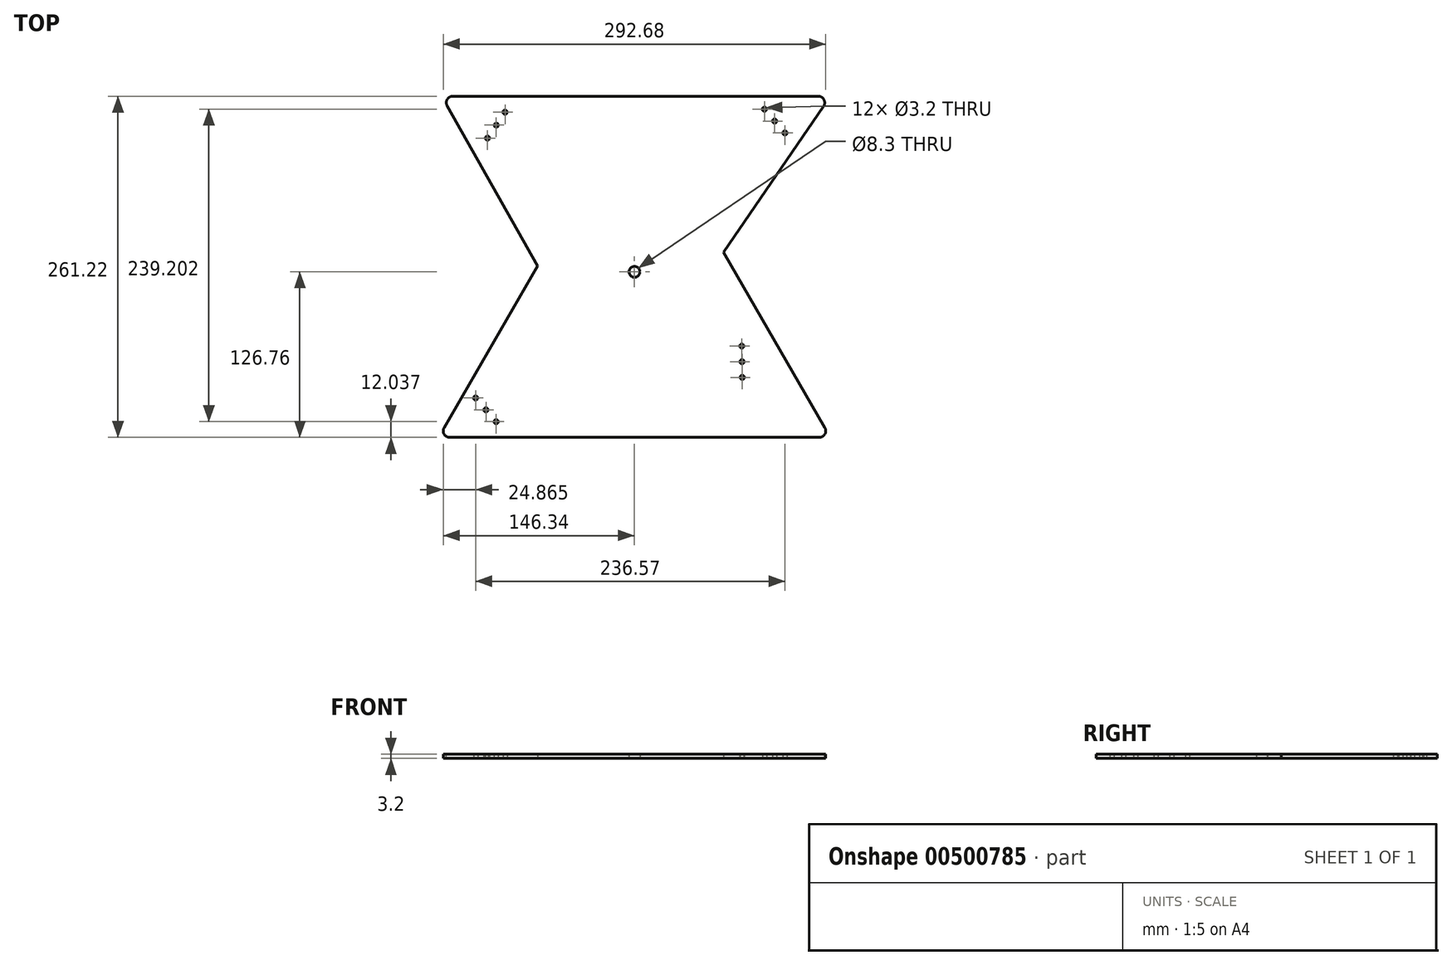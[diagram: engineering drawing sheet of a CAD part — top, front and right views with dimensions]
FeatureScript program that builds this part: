
annotation { "Feature Type Name" : "Feature", "Feature Type Description" : "" }
export const myFeature = defineFeature(function(context is Context, id is Id, definition is map)
    precondition{}
    {
        {
            var Q0;
            Q0=qCreatedBy(makeId("Top.planeOp"),FACE);
            var sketch = newSketch(context, id + "F0", { "sketchPlane" : qUnion([Q0])});
            skLineSegment(sketch, "E0", {"start": v(-150, -126.76) * mm, "end": v(150, -126.76) * mm});
            skLineSegment(sketch, "E1", {"start": v(-150, -126.76) * mm, "end": v(0, 133.04) * mm});
            skLineSegment(sketch, "E2", {"start": v(0, 133.04) * mm, "end": v(150, -126.76) * mm});
            skLineSegment(sketch, "E3.top", {"start": v(-147.51, 134.46) * mm, "end": v(150, 134.46) * mm});
            skCircle(sketch, "E4", {"center": v(0, 0) * mm, "radius": 55 * mm});
            skCircle(sketch, "E5", {"center": v(0, 0) * mm, "radius": 4.15 * mm});
            skLineSegment(sketch, "E6", {"start": v(-150, -126.76) * mm, "end": v(-74.17, 4.58) * mm});
            skLineSegment(sketch, "E7", {"start": v(-74.17, 4.58) * mm, "end": v(0, 133.04) * mm});
            skLineSegment(sketch, "E8", {"start": v(-147.51, 134.46) * mm, "end": v(-74.17, 4.58) * mm});
            skLineSegment(sketch, "E9", {"start": v(-74.17, 4.58) * mm, "end": v(0, -126.76) * mm});
            skLineSegment(sketch, "E10", {"start": v(0, -126.76) * mm, "end": v(68.22, 14.9) * mm});
            skLineSegment(sketch, "E11", {"start": v(68.22, 14.9) * mm, "end": v(150, 134.46) * mm});
            skLineSegment(sketch, "E12", {"start": v(-103.6, 96.31) * mm, "end": v(-121.38, 108.4) * mm});
            skLineSegment(sketch, "E13", {"start": v(-121.38, 108.4) * mm, "end": v(-107.89, 128.24) * mm});
            skLineSegment(sketch, "E14", {"start": v(-90.1, 116.16) * mm, "end": v(-107.89, 128.24) * mm});
            skLineSegment(sketch, "E15", {"start": v(-103.6, 96.31) * mm, "end": v(-90.1, 116.16) * mm});
            skLineSegment(sketch, "E16", {"start": v(-114.63, 118.32) * mm, "end": v(-96.85, 106.24) * mm});
            skLineSegment(sketch, "E17", {"start": v(-99, 122.2) * mm, "end": v(-112.49, 102.35) * mm});
            skCircle(sketch, "E18", {"center": v(-105.74, 112.28) * mm, "radius": 1.6 * mm});
            skCircle(sketch, "E19", {"center": v(-99, 122.2) * mm, "radius": 1.6 * mm});
            skCircle(sketch, "E20", {"center": v(-112.49, 102.35) * mm, "radius": 1.6 * mm});
            skLineSegment(sketch, "E21", {"start": v(-97.65, -107.7) * mm, "end": v(-113.93, -121.75) * mm});
            skLineSegment(sketch, "E22", {"start": v(-113.93, -121.75) * mm, "end": v(-129.61, -103.58) * mm});
            skLineSegment(sketch, "E23", {"start": v(-113.34, -89.53) * mm, "end": v(-129.61, -103.58) * mm});
            skLineSegment(sketch, "E24", {"start": v(-97.65, -107.7) * mm, "end": v(-113.34, -89.53) * mm});
            skLineSegment(sketch, "E25", {"start": v(-121.77, -112.66) * mm, "end": v(-105.5, -98.61) * mm});
            skLineSegment(sketch, "E26", {"start": v(-121.47, -96.56) * mm, "end": v(-105.8, -114.72) * mm});
            skCircle(sketch, "E27", {"center": v(-113.63, -105.64) * mm, "radius": 1.6 * mm});
            skCircle(sketch, "E28", {"center": v(-121.47, -96.56) * mm, "radius": 1.6 * mm});
            skCircle(sketch, "E29", {"center": v(-105.8, -114.72) * mm, "radius": 1.6 * mm});
            skLineSegment(sketch, "E30", {"start": v(123.23, 113.34) * mm, "end": v(106.96, 99.29) * mm});
            skLineSegment(sketch, "E31", {"start": v(106.96, 99.29) * mm, "end": v(91.28, 117.45) * mm});
            skLineSegment(sketch, "E32", {"start": v(107.55, 131.5) * mm, "end": v(91.28, 117.45) * mm});
            skLineSegment(sketch, "E33", {"start": v(123.23, 113.34) * mm, "end": v(107.55, 131.5) * mm});
            skLineSegment(sketch, "E34", {"start": v(99.12, 108.37) * mm, "end": v(115.4, 122.42) * mm});
            skLineSegment(sketch, "E35", {"start": v(99.41, 124.48) * mm, "end": v(115.1, 106.31) * mm});
            skCircle(sketch, "E36", {"center": v(107.25, 115.4) * mm, "radius": 1.6 * mm});
            skCircle(sketch, "E37", {"center": v(99.41, 124.48) * mm, "radius": 1.6 * mm});
            skCircle(sketch, "E38", {"center": v(115.1, 106.31) * mm, "radius": 1.6 * mm});
            skCircle(sketch, "E39", {"center": v(82.28, -68.83) * mm, "radius": 1.6 * mm});
            skCircle(sketch, "E40", {"center": v(82.11, -56.83) * mm, "radius": 1.6 * mm});
            skCircle(sketch, "E41", {"center": v(82.45, -80.83) * mm, "radius": 1.6 * mm});
            skSolve(sketch);
        }
        {
            var Q0;
            {var subQ0=sQuery(id+"F0.wireOp",EDGE,"E3.bottom");var subQ1=sQuery(id+"F0.wireOp",EDGE,"E1");var subQ2=makeQuery(id+"F0.imprint","INTERSECT",VERTEX,{"derivedFrom":[subQ1,subQ0]});Q0=makeQuery(id+"F0.imprint","IMPRINT",FACE,{"disambiguationData":[TD([[makeQuery(id+"F0.imprint","IMPRINT",EDGE,{"disambiguationData":[TD([[subQ2,-1.0]])],"derivedFrom":subQ1}),-1.0]])]});}
            var Q1;
            {var subQ0=sQuery(id+"F0.wireOp",EDGE,"E4");var subQ1=sQuery(id+"F0.wireOp",EDGE,"E1");var subQ2=makeQuery(id+"F0.imprint","INTERSECT",VERTEX,{"disambiguationData":[OD(0.0)],"derivedFrom":[subQ1,subQ0]});Q1=makeQuery(id+"F0.imprint","IMPRINT",FACE,{"disambiguationData":[TD([[makeQuery(id+"F0.imprint","IMPRINT",EDGE,{"disambiguationData":[TD([[subQ2,-1.0]])],"derivedFrom":subQ1}),1.0]])]});}
            var Q2;
            {var subQ0=sQuery(id+"F0.wireOp",EDGE,"E4");var subQ1=sQuery(id+"F0.wireOp",EDGE,"E2");var subQ2=makeQuery(id+"F0.imprint","INTERSECT",VERTEX,{"disambiguationData":[OD(0.0)],"derivedFrom":[subQ1,subQ0]});Q2=makeQuery(id+"F0.imprint","IMPRINT",FACE,{"disambiguationData":[TD([[makeQuery(id+"F0.imprint","IMPRINT",EDGE,{"disambiguationData":[TD([[subQ2,1.0]])],"derivedFrom":subQ1}),1.0]])]});}
            var Q3;
            {var subQ0=sQuery(id+"F0.wireOp",EDGE,"E3.bottom");var subQ1=sQuery(id+"F0.wireOp",EDGE,"E2");var subQ2=makeQuery(id+"F0.imprint","INTERSECT",VERTEX,{"derivedFrom":[subQ1,subQ0]});Q3=makeQuery(id+"F0.imprint","IMPRINT",FACE,{"disambiguationData":[TD([[makeQuery(id+"F0.imprint","IMPRINT",EDGE,{"disambiguationData":[TD([[subQ2,1.0]])],"derivedFrom":subQ1}),-1.0]])]});}
            var Q4;
            {var subQ1=sQuery(id+"F0.wireOp",EDGE,"rkFMjEgM-NqXY-omBp-b8pJ-evcCWdkULaWJ");var subQ3=sQuery(id+"F0.wireOp",EDGE,"E4");var subQ4=makeQuery(id+"F0.imprint","INTERSECT",VERTEX,{"disambiguationData":[OD(1.0)],"derivedFrom":[subQ1,subQ3]});Q4=makeQuery(id+"F0.imprint","IMPRINT",FACE,{"disambiguationData":[TD([[makeQuery(id+"F0.imprint","IMPRINT",EDGE,{"disambiguationData":[TD([[subQ4,-1.0]])],"derivedFrom":subQ3}),-1.0]])]});}
            var Q5;
            {var subQ1=sQuery(id+"F0.wireOp",EDGE,"cOxABnS7-H8AW-JM4u-R3lf-1G958eR7zzaA");var subQ3=sQuery(id+"F0.wireOp",EDGE,"E4");var subQ4=makeQuery(id+"F0.imprint","INTERSECT",VERTEX,{"disambiguationData":[OD(1.0)],"derivedFrom":[subQ1,subQ3]});Q5=makeQuery(id+"F0.imprint","IMPRINT",FACE,{"disambiguationData":[TD([[makeQuery(id+"F0.imprint","IMPRINT",EDGE,{"disambiguationData":[TD([[subQ4,-1.0]])],"derivedFrom":subQ3}),-1.0]])]});}
            var Q6;
            {var subQ1=sQuery(id+"F0.wireOp",EDGE,"E3.top");Q6=makeQuery(id+"F0.imprint","IMPRINT",FACE,{"disambiguationData":[TD([[makeQuery(id+"F0.imprint","IMPRINT",EDGE,{"derivedFrom":subQ1}),-1.0]])]});}
            var Q7;
            {var subQ1=sQuery(id+"F0.wireOp",EDGE,"E1");var subQ3=sQuery(id+"F0.wireOp",EDGE,"E4");var subQ4=makeQuery(id+"F0.imprint","INTERSECT",VERTEX,{"disambiguationData":[OD(1.0)],"derivedFrom":[subQ1,subQ3]});Q7=makeQuery(id+"F0.imprint","IMPRINT",FACE,{"disambiguationData":[TD([[makeQuery(id+"F0.imprint","IMPRINT",EDGE,{"disambiguationData":[TD([[subQ4,1.0]])],"derivedFrom":subQ3}),-1.0]])]});}
            var Q8;
            {var subQ1=sQuery(id+"F0.wireOp",EDGE,"E2");var subQ3=sQuery(id+"F0.wireOp",EDGE,"E4");var subQ4=makeQuery(id+"F0.imprint","INTERSECT",VERTEX,{"disambiguationData":[OD(1.0)],"derivedFrom":[subQ1,subQ3]});Q8=makeQuery(id+"F0.imprint","IMPRINT",FACE,{"disambiguationData":[TD([[makeQuery(id+"F0.imprint","IMPRINT",EDGE,{"disambiguationData":[TD([[subQ4,-1.0]])],"derivedFrom":subQ3}),-1.0]])]});}
            var Q9;
            {var subQ24=sQuery(id+"F0.wireOp",EDGE,"3a51rPi0-I0Z5-NmN3-UwWW-pAn3P1ib9wdr");Q9=makeQuery(id+"F0.imprint","IMPRINT",FACE,{"disambiguationData":[TD([[makeQuery(id+"F0.imprint","IMPRINT",EDGE,{"derivedFrom":subQ24}),-1.0]])]});}
            var Q10;
            {var subQ1=sQuery(id+"F0.wireOp",EDGE,"fhWdT4TT-t5z4-IOB7-9m6H-m55lK3yafObH");var subQ6=sQuery(id+"F0.wireOp",EDGE,"V1MSOyJx-UlwA-KniW-Hypj-Iz20MsfqlTOy");var subQ9=makeQuery(id+"F0.imprint","INTERSECT",VERTEX,{"derivedFrom":[subQ6,subQ1]});Q10=makeQuery(id+"F0.imprint","IMPRINT",FACE,{"disambiguationData":[TD([[makeQuery(id+"F0.imprint","IMPRINT",EDGE,{"disambiguationData":[TD([[subQ9,1.0]])],"derivedFrom":subQ6}),-1.0]])]});}
            var Q11;
            {var subQ0=sQuery(id+"F0.wireOp",EDGE,"YwnaRzwQ-0DJ0-LU4o-7aIr-p4F8uUAJ6yCD");var subQ1=sQuery(id+"F0.wireOp",EDGE,"fhWdT4TT-t5z4-IOB7-9m6H-m55lK3yafObH");var subQ2=makeQuery(id+"F0.imprint","INTERSECT",VERTEX,{"derivedFrom":[subQ1,subQ0]});Q11=makeQuery(id+"F0.imprint","IMPRINT",FACE,{"disambiguationData":[TD([[makeQuery(id+"F0.imprint","IMPRINT",EDGE,{"disambiguationData":[TD([[subQ2,-1.0]])],"derivedFrom":subQ1}),1.0]])]});}
            var Q12;
            {var subQ1=sQuery(id+"F0.wireOp",EDGE,"fhWdT4TT-t5z4-IOB7-9m6H-m55lK3yafObH");var subQ5=sQuery(id+"F0.wireOp",EDGE,"YwnaRzwQ-0DJ0-LU4o-7aIr-p4F8uUAJ6yCD");var subQ6=makeQuery(id+"F0.imprint","INTERSECT",VERTEX,{"derivedFrom":[subQ1,subQ5]});Q12=makeQuery(id+"F0.imprint","IMPRINT",FACE,{"disambiguationData":[TD([[makeQuery(id+"F0.imprint","IMPRINT",EDGE,{"disambiguationData":[TD([[subQ6,1.0]])],"derivedFrom":subQ1}),1.0]])]});}
            var Q13;
            {var subQ3=sQuery(id+"F0.wireOp",EDGE,"ZtclyvMB-XdF3-0tLt-WoJ9-w7VQqLJZLKuw");var subQ7=sQuery(id+"F0.wireOp",EDGE,"sQT1DKzU-x4bm-HVrY-kuNr-4rAKIQ2P2SoH");var subQ9=makeQuery(id+"F0.imprint","INTERSECT",VERTEX,{"disambiguationData":[OD(1.0)],"derivedFrom":[subQ7,subQ3]});Q13=makeQuery(id+"F0.imprint","IMPRINT",FACE,{"disambiguationData":[TD([[makeQuery(id+"F0.imprint","IMPRINT",EDGE,{"disambiguationData":[TD([[subQ9,-1.0]])],"derivedFrom":subQ7}),1.0]])]});}
            var Q14;
            {var subQ1=sQuery(id+"F0.wireOp",EDGE,"lj4hX3Zr-Y8O4-Ni6O-LBAL-KsnYeP7ui8yA");var subQ5=sQuery(id+"F0.wireOp",EDGE,"8QxvuuJz-OpXC-lB6l-rkeD-zr6WuXKeRFd8");var subQ6=makeQuery(id+"F0.imprint","INTERSECT",VERTEX,{"derivedFrom":[subQ1,subQ5]});Q14=makeQuery(id+"F0.imprint","IMPRINT",FACE,{"disambiguationData":[TD([[makeQuery(id+"F0.imprint","IMPRINT",EDGE,{"disambiguationData":[TD([[subQ6,-1.0]])],"derivedFrom":subQ1}),-1.0]])]});}
            var Q15;
            {var subQ5=sQuery(id+"F0.wireOp",EDGE,"YwnaRzwQ-0DJ0-LU4o-7aIr-p4F8uUAJ6yCD");var subQ7=sQuery(id+"F0.wireOp",EDGE,"sQT1DKzU-x4bm-HVrY-kuNr-4rAKIQ2P2SoH");var subQ8=makeQuery(id+"F0.imprint","INTERSECT",VERTEX,{"derivedFrom":[subQ7,subQ5]});Q15=makeQuery(id+"F0.imprint","IMPRINT",FACE,{"disambiguationData":[TD([[makeQuery(id+"F0.imprint","IMPRINT",EDGE,{"disambiguationData":[TD([[subQ8,-1.0]])],"derivedFrom":subQ7}),1.0]])]});}
            var Q16;
            {var subQ1=sQuery(id+"F0.wireOp",EDGE,"lj4hX3Zr-Y8O4-Ni6O-LBAL-KsnYeP7ui8yA");var subQ6=sQuery(id+"F0.wireOp",EDGE,"V1MSOyJx-UlwA-KniW-Hypj-Iz20MsfqlTOy");var subQ9=makeQuery(id+"F0.imprint","INTERSECT",VERTEX,{"derivedFrom":[subQ1,subQ6]});Q16=makeQuery(id+"F0.imprint","IMPRINT",FACE,{"disambiguationData":[TD([[makeQuery(id+"F0.imprint","IMPRINT",EDGE,{"disambiguationData":[TD([[subQ9,1.0]])],"derivedFrom":subQ1}),-1.0]])]});}
            var Q17;
            {var subQ0=sQuery(id+"F0.wireOp",EDGE,"E4");var subQ1=sQuery(id+"F0.wireOp",EDGE,"E1");var subQ2=makeQuery(id+"F0.imprint","INTERSECT",VERTEX,{"disambiguationData":[OD(0.0)],"derivedFrom":[subQ1,subQ0]});Q17=makeQuery(id+"F0.imprint","IMPRINT",FACE,{"disambiguationData":[TD([[makeQuery(id+"F0.imprint","IMPRINT",EDGE,{"disambiguationData":[TD([[subQ2,-1.0]])],"derivedFrom":subQ1}),-1.0]])]});}
            var Q18;
            {var subQ1=sQuery(id+"F0.wireOp",EDGE,"E1");var subQ6=sQuery(id+"F0.wireOp",EDGE,"rkFMjEgM-NqXY-omBp-b8pJ-evcCWdkULaWJ");var subQ7=makeQuery(id+"F0.imprint","INTERSECT",VERTEX,{"derivedFrom":[subQ1,subQ6]});Q18=makeQuery(id+"F0.imprint","IMPRINT",FACE,{"disambiguationData":[TD([[makeQuery(id+"F0.imprint","IMPRINT",EDGE,{"disambiguationData":[TD([[subQ7,-1.0]])],"derivedFrom":subQ1}),-1.0]])]});}
            var Q19;
            {var subQ0=sQuery(id+"F0.wireOp",EDGE,"E4");var subQ1=sQuery(id+"F0.wireOp",EDGE,"E2");var subQ2=makeQuery(id+"F0.imprint","INTERSECT",VERTEX,{"disambiguationData":[OD(1.0)],"derivedFrom":[subQ1,subQ0]});Q19=makeQuery(id+"F0.imprint","IMPRINT",FACE,{"disambiguationData":[TD([[makeQuery(id+"F0.imprint","IMPRINT",EDGE,{"disambiguationData":[TD([[subQ2,-1.0]])],"derivedFrom":subQ1}),-1.0]])]});}
            var Q20;
            {var subQ0=sQuery(id+"F0.wireOp",EDGE,"E4");var subQ1=sQuery(id+"F0.wireOp",EDGE,"E2");var subQ2=makeQuery(id+"F0.imprint","INTERSECT",VERTEX,{"disambiguationData":[OD(0.0)],"derivedFrom":[subQ1,subQ0]});Q20=makeQuery(id+"F0.imprint","IMPRINT",FACE,{"disambiguationData":[TD([[makeQuery(id+"F0.imprint","IMPRINT",EDGE,{"disambiguationData":[TD([[subQ2,1.0]])],"derivedFrom":subQ1}),-1.0]])]});}
            var Q21;
            {var subQ0=sQuery(id+"F0.wireOp",EDGE,"E4");var subQ1=sQuery(id+"F0.wireOp",EDGE,"E2");var subQ2=makeQuery(id+"F0.imprint","INTERSECT",VERTEX,{"disambiguationData":[OD(1.0)],"derivedFrom":[subQ1,subQ0]});Q21=makeQuery(id+"F0.imprint","IMPRINT",FACE,{"disambiguationData":[TD([[makeQuery(id+"F0.imprint","IMPRINT",EDGE,{"disambiguationData":[TD([[subQ2,-1.0]])],"derivedFrom":subQ1}),1.0]])]});}
            var Q22;
            {var subQ0=sQuery(id+"F0.wireOp",EDGE,"rkFMjEgM-NqXY-omBp-b8pJ-evcCWdkULaWJ");var subQ1=sQuery(id+"F0.wireOp",EDGE,"E1");var subQ2=makeQuery(id+"F0.imprint","INTERSECT",VERTEX,{"derivedFrom":[subQ1,subQ0]});Q22=makeQuery(id+"F0.imprint","IMPRINT",FACE,{"disambiguationData":[TD([[makeQuery(id+"F0.imprint","IMPRINT",EDGE,{"disambiguationData":[TD([[subQ2,-1.0]])],"derivedFrom":subQ1}),1.0]])]});}
            var Q23;
            {var subQ1=sQuery(id+"F0.wireOp",EDGE,"40212db6-d506-4749-b9d6-5a5c076448ad");var subQ6=sQuery(id+"F0.wireOp",EDGE,"c31b4b8a-1931-4577-9c9e-ab941fa55453");var subQ9=makeQuery(id+"F0.imprint","INTERSECT",VERTEX,{"derivedFrom":[subQ6,subQ1]});Q23=makeQuery(id+"F0.imprint","IMPRINT",FACE,{"disambiguationData":[TD([[makeQuery(id+"F0.imprint","IMPRINT",EDGE,{"disambiguationData":[TD([[subQ9,-1.0]])],"derivedFrom":subQ6}),1.0]])]});}
            var Q24;
            {var subQ1=sQuery(id+"F0.wireOp",EDGE,"40212db6-d506-4749-b9d6-5a5c076448ad");var subQ5=sQuery(id+"F0.wireOp",EDGE,"e9d3f93f-f6a2-4b0d-aba8-6108448f5a32");var subQ6=makeQuery(id+"F0.imprint","INTERSECT",VERTEX,{"derivedFrom":[subQ5,subQ1]});Q24=makeQuery(id+"F0.imprint","IMPRINT",FACE,{"disambiguationData":[TD([[makeQuery(id+"F0.imprint","IMPRINT",EDGE,{"disambiguationData":[TD([[subQ6,-1.0]])],"derivedFrom":subQ5}),-1.0]])]});}
            var Q25;
            {var subQ1=sQuery(id+"F0.wireOp",EDGE,"e9d3f93f-f6a2-4b0d-aba8-6108448f5a32");var subQ6=sQuery(id+"F0.wireOp",EDGE,"c1a090f9-9c0e-4005-906d-b8579f657efc");var subQ9=makeQuery(id+"F0.imprint","INTERSECT",VERTEX,{"derivedFrom":[subQ1,subQ6]});Q25=makeQuery(id+"F0.imprint","IMPRINT",FACE,{"disambiguationData":[TD([[makeQuery(id+"F0.imprint","IMPRINT",EDGE,{"disambiguationData":[TD([[subQ9,1.0]])],"derivedFrom":subQ1}),-1.0]])]});}
            var Q26;
            {var subQ1=sQuery(id+"F0.wireOp",EDGE,"c31b4b8a-1931-4577-9c9e-ab941fa55453");var subQ5=sQuery(id+"F0.wireOp",EDGE,"c1a090f9-9c0e-4005-906d-b8579f657efc");var subQ6=makeQuery(id+"F0.imprint","INTERSECT",VERTEX,{"derivedFrom":[subQ5,subQ1]});Q26=makeQuery(id+"F0.imprint","IMPRINT",FACE,{"disambiguationData":[TD([[makeQuery(id+"F0.imprint","IMPRINT",EDGE,{"disambiguationData":[TD([[subQ6,1.0]])],"derivedFrom":subQ5}),-1.0]])]});}
            var Q27;
            {var subQ1=sQuery(id+"F0.wireOp",EDGE,"1460a9e2-be03-4b2d-ab73-b3bdc3734335");var subQ5=sQuery(id+"F0.wireOp",EDGE,"b409e4f6-961d-4708-9ecc-1fc577be94c4");var subQ6=makeQuery(id+"F0.imprint","INTERSECT",VERTEX,{"derivedFrom":[subQ5,subQ1]});Q27=makeQuery(id+"F0.imprint","IMPRINT",FACE,{"disambiguationData":[TD([[makeQuery(id+"F0.imprint","IMPRINT",EDGE,{"disambiguationData":[TD([[subQ6,1.0]])],"derivedFrom":subQ5}),-1.0]])]});}
            var Q28;
            {var subQ1=sQuery(id+"F0.wireOp",EDGE,"1460a9e2-be03-4b2d-ab73-b3bdc3734335");var subQ5=sQuery(id+"F0.wireOp",EDGE,"d7addea2-58b3-402f-bf6f-7ffec54a4836");var subQ6=makeQuery(id+"F0.imprint","INTERSECT",VERTEX,{"derivedFrom":[subQ1,subQ5]});Q28=makeQuery(id+"F0.imprint","IMPRINT",FACE,{"disambiguationData":[TD([[makeQuery(id+"F0.imprint","IMPRINT",EDGE,{"disambiguationData":[TD([[subQ6,1.0]])],"derivedFrom":subQ1}),-1.0]])]});}
            var Q29;
            {var subQ1=sQuery(id+"F0.wireOp",EDGE,"LilHJE2K-ZwTa-264l-AHjR-kb1P9RslV9pw");var subQ6=sQuery(id+"F0.wireOp",EDGE,"d7addea2-58b3-402f-bf6f-7ffec54a4836");var subQ9=makeQuery(id+"F0.imprint","INTERSECT",VERTEX,{"derivedFrom":[subQ6,subQ1]});Q29=makeQuery(id+"F0.imprint","IMPRINT",FACE,{"disambiguationData":[TD([[makeQuery(id+"F0.imprint","IMPRINT",EDGE,{"disambiguationData":[TD([[subQ9,-1.0]])],"derivedFrom":subQ6}),1.0]])]});}
            var Q30;
            {var subQ1=sQuery(id+"F0.wireOp",EDGE,"b409e4f6-961d-4708-9ecc-1fc577be94c4");var subQ6=sQuery(id+"F0.wireOp",EDGE,"LilHJE2K-ZwTa-264l-AHjR-kb1P9RslV9pw");var subQ9=makeQuery(id+"F0.imprint","INTERSECT",VERTEX,{"derivedFrom":[subQ1,subQ6]});Q30=makeQuery(id+"F0.imprint","IMPRINT",FACE,{"disambiguationData":[TD([[makeQuery(id+"F0.imprint","IMPRINT",EDGE,{"disambiguationData":[TD([[subQ9,-1.0]])],"derivedFrom":subQ1}),-1.0]])]});}
            var Q31;
            {var subQ1=sQuery(id+"F0.wireOp",EDGE,"3a5bb0a6-3794-4467-a787-e42bd4ee81f6");var subQ5=sQuery(id+"F0.wireOp",EDGE,"1a2aea71-d40e-4995-b3ae-06d99a898208");var subQ6=makeQuery(id+"F0.imprint","INTERSECT",VERTEX,{"derivedFrom":[subQ5,subQ1]});Q31=makeQuery(id+"F0.imprint","IMPRINT",FACE,{"disambiguationData":[TD([[makeQuery(id+"F0.imprint","IMPRINT",EDGE,{"disambiguationData":[TD([[subQ6,1.0]])],"derivedFrom":subQ5}),-1.0]])]});}
            var Q32;
            {var subQ1=sQuery(id+"F0.wireOp",EDGE,"b805471b-5294-4ecf-8a37-7c4feab366c0");var subQ6=sQuery(id+"F0.wireOp",EDGE,"1a2aea71-d40e-4995-b3ae-06d99a898208");var subQ9=makeQuery(id+"F0.imprint","INTERSECT",VERTEX,{"derivedFrom":[subQ1,subQ6]});Q32=makeQuery(id+"F0.imprint","IMPRINT",FACE,{"disambiguationData":[TD([[makeQuery(id+"F0.imprint","IMPRINT",EDGE,{"disambiguationData":[TD([[subQ9,1.0]])],"derivedFrom":subQ1}),-1.0]])]});}
            var Q33;
            {var subQ1=sQuery(id+"F0.wireOp",EDGE,"df8aa925-b617-4437-be64-db43ea589b33");var subQ5=sQuery(id+"F0.wireOp",EDGE,"b805471b-5294-4ecf-8a37-7c4feab366c0");var subQ6=makeQuery(id+"F0.imprint","INTERSECT",VERTEX,{"derivedFrom":[subQ5,subQ1]});Q33=makeQuery(id+"F0.imprint","IMPRINT",FACE,{"disambiguationData":[TD([[makeQuery(id+"F0.imprint","IMPRINT",EDGE,{"disambiguationData":[TD([[subQ6,-1.0]])],"derivedFrom":subQ5}),-1.0]])]});}
            var Q34;
            {var subQ1=sQuery(id+"F0.wireOp",EDGE,"df8aa925-b617-4437-be64-db43ea589b33");var subQ6=sQuery(id+"F0.wireOp",EDGE,"3a5bb0a6-3794-4467-a787-e42bd4ee81f6");var subQ9=makeQuery(id+"F0.imprint","INTERSECT",VERTEX,{"derivedFrom":[subQ6,subQ1]});Q34=makeQuery(id+"F0.imprint","IMPRINT",FACE,{"disambiguationData":[TD([[makeQuery(id+"F0.imprint","IMPRINT",EDGE,{"disambiguationData":[TD([[subQ9,-1.0]])],"derivedFrom":subQ6}),1.0]])]});}
            var Q35;
            {var subQ1=sQuery(id+"F0.wireOp",EDGE,"60477fe5-d128-4377-a6e9-975c3c0ee1ff");var subQ6=sQuery(id+"F0.wireOp",EDGE,"9af5a659-fb0b-4865-b0cf-d8a56090b59d");var subQ9=makeQuery(id+"F0.imprint","INTERSECT",VERTEX,{"derivedFrom":[subQ6,subQ1]});Q35=makeQuery(id+"F0.imprint","IMPRINT",FACE,{"disambiguationData":[TD([[makeQuery(id+"F0.imprint","IMPRINT",EDGE,{"disambiguationData":[TD([[subQ9,-1.0]])],"derivedFrom":subQ6}),1.0]])]});}
            var Q36;
            {var subQ1=sQuery(id+"F0.wireOp",EDGE,"9af5a659-fb0b-4865-b0cf-d8a56090b59d");var subQ5=sQuery(id+"F0.wireOp",EDGE,"795894dc-45e6-44b4-9a82-fe3d4ca950ed");var subQ6=makeQuery(id+"F0.imprint","INTERSECT",VERTEX,{"derivedFrom":[subQ5,subQ1]});Q36=makeQuery(id+"F0.imprint","IMPRINT",FACE,{"disambiguationData":[TD([[makeQuery(id+"F0.imprint","IMPRINT",EDGE,{"disambiguationData":[TD([[subQ6,1.0]])],"derivedFrom":subQ5}),-1.0]])]});}
            var Q37;
            {var subQ1=sQuery(id+"F0.wireOp",EDGE,"7ff22509-a0f6-46b4-94aa-8c69f69d7618");var subQ6=sQuery(id+"F0.wireOp",EDGE,"795894dc-45e6-44b4-9a82-fe3d4ca950ed");var subQ9=makeQuery(id+"F0.imprint","INTERSECT",VERTEX,{"derivedFrom":[subQ1,subQ6]});Q37=makeQuery(id+"F0.imprint","IMPRINT",FACE,{"disambiguationData":[TD([[makeQuery(id+"F0.imprint","IMPRINT",EDGE,{"disambiguationData":[TD([[subQ9,1.0]])],"derivedFrom":subQ1}),-1.0]])]});}
            var Q38;
            {var subQ1=sQuery(id+"F0.wireOp",EDGE,"60477fe5-d128-4377-a6e9-975c3c0ee1ff");var subQ5=sQuery(id+"F0.wireOp",EDGE,"7ff22509-a0f6-46b4-94aa-8c69f69d7618");var subQ6=makeQuery(id+"F0.imprint","INTERSECT",VERTEX,{"derivedFrom":[subQ5,subQ1]});Q38=makeQuery(id+"F0.imprint","IMPRINT",FACE,{"disambiguationData":[TD([[makeQuery(id+"F0.imprint","IMPRINT",EDGE,{"disambiguationData":[TD([[subQ6,-1.0]])],"derivedFrom":subQ5}),-1.0]])]});}
            var Q39;
            {var subQ9=sQuery(id+"F0.wireOp",EDGE,"E1");var subQ10=sQuery(id+"F0.wireOp",EDGE,"E0");var subQ11=makeQuery(id+"F0.imprint","INTERSECT",VERTEX,{"derivedFrom":[subQ10,subQ9]});Q39=makeQuery(id+"F0.imprint","IMPRINT",FACE,{"disambiguationData":[TD([[makeQuery(id+"F0.imprint","IMPRINT",EDGE,{"disambiguationData":[TD([[subQ11,-1.0]])],"derivedFrom":subQ9}),-1.0]])]});}
            var Q40;
            {var subQ5=sQuery(id+"F0.wireOp",EDGE,"E2");var subQ6=sQuery(id+"F0.wireOp",EDGE,"E0");var subQ7=makeQuery(id+"F0.imprint","INTERSECT",VERTEX,{"derivedFrom":[subQ6,subQ5]});Q40=makeQuery(id+"F0.imprint","IMPRINT",FACE,{"disambiguationData":[TD([[makeQuery(id+"F0.imprint","IMPRINT",EDGE,{"disambiguationData":[TD([[subQ7,1.0]])],"derivedFrom":subQ5}),-1.0]])]});}
            var Q41;
            Q41=makeQuery(id+"F0.imprint","IMPRINT",FACE,{"disambiguationData":[TD([[makeQuery(id+"F0.imprint","IMPRINT",EDGE,{"derivedFrom":sQuery(id+"F0.wireOp",EDGE,"E4")}),1.0]])]});
            var Q42;
            {var subQ16=sQuery(id+"F0.wireOp",EDGE,"E6");Q42=makeQuery(id+"F0.imprint","IMPRINT",FACE,{"disambiguationData":[TD([[makeQuery(id+"F0.imprint","IMPRINT",EDGE,{"derivedFrom":subQ16}),-1.0]])]});}
            var Q43;
            {var subQ5=sQuery(id+"F0.wireOp",EDGE,"E24");var subQ6=sQuery(id+"F0.wireOp",EDGE,"E23");var subQ7=makeQuery(id+"F0.imprint","INTERSECT",VERTEX,{"derivedFrom":[subQ6,subQ5]});Q43=makeQuery(id+"F0.imprint","IMPRINT",FACE,{"disambiguationData":[TD([[makeQuery(id+"F0.imprint","IMPRINT",EDGE,{"disambiguationData":[TD([[subQ7,-1.0]])],"derivedFrom":subQ6}),1.0]])]});}
            var Q44;
            {var subQ6=sQuery(id+"F0.wireOp",EDGE,"E24");var subQ9=sQuery(id+"F0.wireOp",EDGE,"E21");var subQ10=makeQuery(id+"F0.imprint","INTERSECT",VERTEX,{"derivedFrom":[subQ9,subQ6]});Q44=makeQuery(id+"F0.imprint","IMPRINT",FACE,{"disambiguationData":[TD([[makeQuery(id+"F0.imprint","IMPRINT",EDGE,{"disambiguationData":[TD([[subQ10,-1.0]])],"derivedFrom":subQ9}),-1.0]])]});}
            var Q45;
            {var subQ6=sQuery(id+"F0.wireOp",EDGE,"E22");var subQ9=sQuery(id+"F0.wireOp",EDGE,"E21");var subQ10=makeQuery(id+"F0.imprint","INTERSECT",VERTEX,{"derivedFrom":[subQ9,subQ6]});Q45=makeQuery(id+"F0.imprint","IMPRINT",FACE,{"disambiguationData":[TD([[makeQuery(id+"F0.imprint","IMPRINT",EDGE,{"disambiguationData":[TD([[subQ10,1.0]])],"derivedFrom":subQ9}),-1.0]])]});}
            var Q46;
            {var subQ6=sQuery(id+"F0.wireOp",EDGE,"E22");var subQ9=sQuery(id+"F0.wireOp",EDGE,"E23");var subQ10=makeQuery(id+"F0.imprint","INTERSECT",VERTEX,{"derivedFrom":[subQ6,subQ9]});Q46=makeQuery(id+"F0.imprint","IMPRINT",FACE,{"disambiguationData":[TD([[makeQuery(id+"F0.imprint","IMPRINT",EDGE,{"disambiguationData":[TD([[subQ10,1.0]])],"derivedFrom":subQ6}),-1.0]])]});}
            var Q47;
            {var subQ6=sQuery(id+"F0.wireOp",EDGE,"E31");var subQ9=sQuery(id+"F0.wireOp",EDGE,"E30");var subQ10=makeQuery(id+"F0.imprint","INTERSECT",VERTEX,{"derivedFrom":[subQ9,subQ6]});Q47=makeQuery(id+"F0.imprint","IMPRINT",FACE,{"disambiguationData":[TD([[makeQuery(id+"F0.imprint","IMPRINT",EDGE,{"disambiguationData":[TD([[subQ10,1.0]])],"derivedFrom":subQ9}),-1.0]])]});}
            var Q48;
            {var subQ6=sQuery(id+"F0.wireOp",EDGE,"E31");var subQ9=sQuery(id+"F0.wireOp",EDGE,"E32");var subQ10=makeQuery(id+"F0.imprint","INTERSECT",VERTEX,{"derivedFrom":[subQ6,subQ9]});Q48=makeQuery(id+"F0.imprint","IMPRINT",FACE,{"disambiguationData":[TD([[makeQuery(id+"F0.imprint","IMPRINT",EDGE,{"disambiguationData":[TD([[subQ10,1.0]])],"derivedFrom":subQ6}),-1.0]])]});}
            var Q49;
            {var subQ5=sQuery(id+"F0.wireOp",EDGE,"E33");var subQ6=sQuery(id+"F0.wireOp",EDGE,"E32");var subQ7=makeQuery(id+"F0.imprint","INTERSECT",VERTEX,{"derivedFrom":[subQ6,subQ5]});Q49=makeQuery(id+"F0.imprint","IMPRINT",FACE,{"disambiguationData":[TD([[makeQuery(id+"F0.imprint","IMPRINT",EDGE,{"disambiguationData":[TD([[subQ7,-1.0]])],"derivedFrom":subQ6}),1.0]])]});}
            var Q50;
            {var subQ6=sQuery(id+"F0.wireOp",EDGE,"E33");var subQ9=sQuery(id+"F0.wireOp",EDGE,"E30");var subQ10=makeQuery(id+"F0.imprint","INTERSECT",VERTEX,{"derivedFrom":[subQ9,subQ6]});Q50=makeQuery(id+"F0.imprint","IMPRINT",FACE,{"disambiguationData":[TD([[makeQuery(id+"F0.imprint","IMPRINT",EDGE,{"disambiguationData":[TD([[subQ10,-1.0]])],"derivedFrom":subQ9}),-1.0]])]});}
            var Q51;
            {var subQ6=sQuery(id+"F0.wireOp",EDGE,"E13");var subQ9=sQuery(id+"F0.wireOp",EDGE,"E14");var subQ10=makeQuery(id+"F0.imprint","INTERSECT",VERTEX,{"derivedFrom":[subQ6,subQ9]});Q51=makeQuery(id+"F0.imprint","IMPRINT",FACE,{"disambiguationData":[TD([[makeQuery(id+"F0.imprint","IMPRINT",EDGE,{"disambiguationData":[TD([[subQ10,1.0]])],"derivedFrom":subQ6}),-1.0]])]});}
            var Q52;
            {var subQ5=sQuery(id+"F0.wireOp",EDGE,"E15");var subQ6=sQuery(id+"F0.wireOp",EDGE,"E14");var subQ7=makeQuery(id+"F0.imprint","INTERSECT",VERTEX,{"derivedFrom":[subQ6,subQ5]});Q52=makeQuery(id+"F0.imprint","IMPRINT",FACE,{"disambiguationData":[TD([[makeQuery(id+"F0.imprint","IMPRINT",EDGE,{"disambiguationData":[TD([[subQ7,-1.0]])],"derivedFrom":subQ6}),1.0]])]});}
            var Q53;
            {var subQ6=sQuery(id+"F0.wireOp",EDGE,"E15");var subQ9=sQuery(id+"F0.wireOp",EDGE,"E12");var subQ10=makeQuery(id+"F0.imprint","INTERSECT",VERTEX,{"derivedFrom":[subQ9,subQ6]});Q53=makeQuery(id+"F0.imprint","IMPRINT",FACE,{"disambiguationData":[TD([[makeQuery(id+"F0.imprint","IMPRINT",EDGE,{"disambiguationData":[TD([[subQ10,-1.0]])],"derivedFrom":subQ9}),-1.0]])]});}
            var Q54;
            {var subQ6=sQuery(id+"F0.wireOp",EDGE,"E13");var subQ9=sQuery(id+"F0.wireOp",EDGE,"E12");var subQ10=makeQuery(id+"F0.imprint","INTERSECT",VERTEX,{"derivedFrom":[subQ9,subQ6]});Q54=makeQuery(id+"F0.imprint","IMPRINT",FACE,{"disambiguationData":[TD([[makeQuery(id+"F0.imprint","IMPRINT",EDGE,{"disambiguationData":[TD([[subQ10,1.0]])],"derivedFrom":subQ9}),-1.0]])]});}
            extrude(context, id + "F1", {"entities" : qUnion([Q0, Q1, Q2, Q3, Q4, Q5, Q6, Q7, Q8, Q9, Q10, Q11, Q12, Q13, Q14, Q15, Q16, Q17, Q18, Q19, Q20, Q21, Q22, Q23, Q24, Q25, Q26, Q27, Q28, Q29, Q30, Q31, Q32, Q33, Q34, Q35, Q36, Q37, Q38, Q39, Q40, Q41, Q42, Q43, Q44, Q45, Q46, Q47, Q48, Q49, Q50, Q51, Q52, Q53, Q54]), "depth" : 3.2 * mm, "offsetDistance" : 25 * mm});
        }
        {
            var Q0;
            Q0=makeQuery(id+"F1.opExtrude","SWEPT_EDGE",EDGE,{"disambiguationData":[OSD([sQuery(id+"F0.wireOp",EDGE,"E3.top"),sQuery(id+"F0.wireOp",EDGE,"SB21cuuP-Ky2W-nH3l-qBr1-9rjchfua6wKX")])]});
            var Q1;
            Q1=makeQuery(id+"F1.opExtrude","SWEPT_EDGE",EDGE,{"disambiguationData":[OSD([sQuery(id+"F0.wireOp",EDGE,"E3.top"),sQuery(id+"F0.wireOp",EDGE,"rkFMjEgM-NqXY-omBp-b8pJ-evcCWdkULaWJ")])]});
            var Q2;
            Q2=makeQuery(id+"F1.opExtrude","SWEPT_EDGE",EDGE,{"disambiguationData":[OSD([sQuery(id+"F0.wireOp",EDGE,"E1"),sQuery(id+"F0.wireOp",EDGE,"E3.bottom")])]});
            var Q3;
            Q3=makeQuery(id+"F1.opExtrude","SWEPT_EDGE",EDGE,{"disambiguationData":[OSD([sQuery(id+"F0.wireOp",EDGE,"E2"),sQuery(id+"F0.wireOp",EDGE,"E3.bottom")])]});
            fillet(context, id + "F2", {"entities" : qUnion([Q0, Q1, Q2, Q3]), "radius" : 5 * mm, "tangentPropagation" : true, "allowEdgeOverflow" : false});
        }
    });
